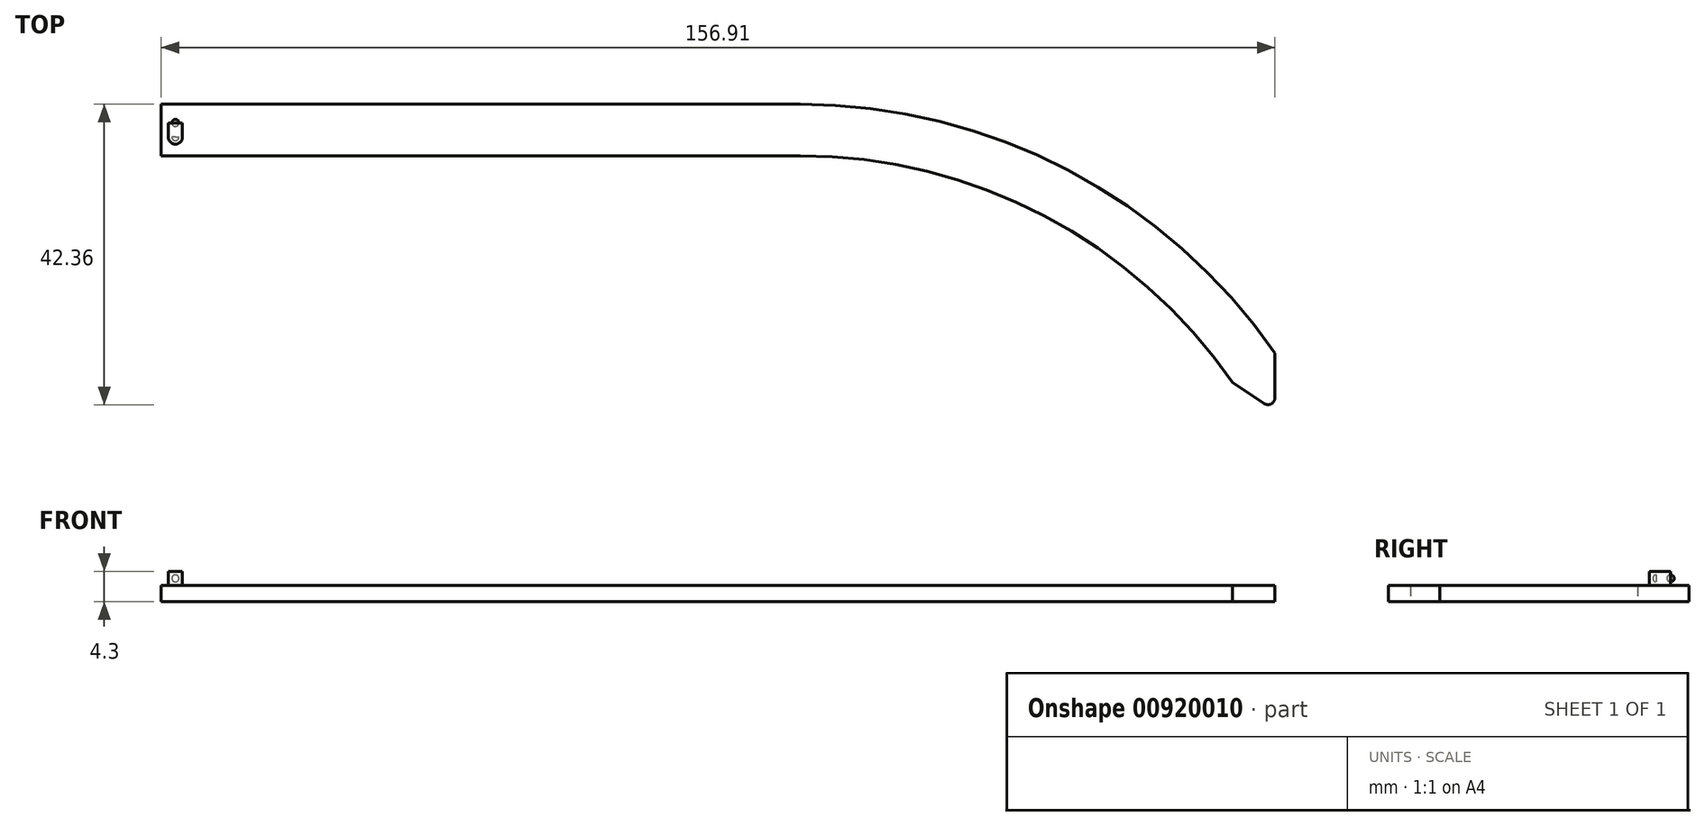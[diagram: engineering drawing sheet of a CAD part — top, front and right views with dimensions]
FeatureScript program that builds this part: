
annotation { "Feature Type Name" : "Feature", "Feature Type Description" : "" }
export const myFeature = defineFeature(function(context is Context, id is Id, definition is map)
    precondition{}
    {
        {
            var Q0;
            Q0=qCreatedBy(makeId("Top.planeOp"),FACE);
            var sketch = newSketch(context, id + "F0", { "sketchPlane" : qUnion([Q0])});
            skLineSegment(sketch, "E0.bottom", {"start": v(-45, 3.62) * mm, "end": v(45, 3.62) * mm});
            skLineSegment(sketch, "E0.top", {"start": v(-45, -3.62) * mm, "end": v(45, -3.62) * mm});
            skLineSegment(sketch, "E0.left", {"start": v(-45, 3.62) * mm, "end": v(-45, -3.62) * mm});
            skLineSegment(sketch, "E0.right", {"start": v(45, 3.62) * mm, "end": v(45, -3.62) * mm});
            skPoint(sketch, "E0.middle", {"position": v(0, 0) * mm});
            skLineSegment(sketch, "E1", {"start": v(45, 20.51) * mm, "end": v(45, -38.93) * mm});
            skArc(sketch, "E2", {"start": v(111.91, -31.5) * mm, "mid": v(82.79, -5.69) * mm, "end": v(45, 3.62) * mm});
            skArc(sketch, "E3.0", {"start": v(105.95, -35.62) * mm, "mid": v(79.42, -12.1) * mm, "end": v(45, -3.62) * mm});
            skLineSegment(sketch, "E4", {"start": v(105.95, -35.62) * mm, "end": v(110.36, -38.57) * mm});
            skLineSegment(sketch, "E5", {"start": v(111.91, -37.75) * mm, "end": v(111.91, -31.5) * mm});
            skPoint(sketch, "E6.visualSharp", {"position": v(111.91, -39.62) * mm});
            skArc(sketch, "E6.filletArc", {"start": v(110.36, -38.57) * mm, "mid": v(111.39, -38.63) * mm, "end": v(111.91, -37.75) * mm});
            skLineSegment(sketch, "E7", {"start": v(-45, 0) * mm, "end": v(-44, 0) * mm});
            skLineSegment(sketch, "E8", {"start": v(-44, 0) * mm, "end": v(-43, 0) * mm});
            skLineSegment(sketch, "E9.bottom", {"start": v(-42, 1) * mm, "end": v(-44, 1) * mm});
            skLineSegment(sketch, "E9.top", {"start": v(-42, -1) * mm, "end": v(-44, -1) * mm});
            skLineSegment(sketch, "E9.left", {"start": v(-42, 1) * mm, "end": v(-42, -1) * mm});
            skLineSegment(sketch, "E9.right", {"start": v(-44, 1) * mm, "end": v(-44, -1) * mm});
            skPoint(sketch, "E9.middle", {"position": v(-43, 0) * mm});
            skSolve(sketch);
        }
        {
            var Q0;
            {var subQ6=sQuery(id+"F0.wireOp",EDGE,"E0.bottom");Q0=makeQuery(id+"F0.imprint","IMPRINT",FACE,{"disambiguationData":[TD([[makeQuery(id+"F0.imprint","IMPRINT",EDGE,{"derivedFrom":subQ6}),-1.0]])]});}
            var Q1;
            Q1=makeQuery(id+"F0.imprint","IMPRINT",FACE,{"disambiguationData":[TD([[makeQuery(id+"F0.imprint","IMPRINT",EDGE,{"derivedFrom":sQuery(id+"F0.wireOp",EDGE,"E0.right")}),1.0]])]});
            var Q2;
            {var subQ3=sQuery(id+"F0.wireOp",EDGE,"E9.bottom");Q2=makeQuery(id+"F0.imprint","IMPRINT",FACE,{"disambiguationData":[TD([[makeQuery(id+"F0.imprint","IMPRINT",EDGE,{"derivedFrom":subQ3}),1.0]])]});}
            extrude(context, id + "F1", {"entities" : qUnion([Q0, Q1, Q2]), "depth" : 2.3 * mm, "offsetDistance" : 25 * mm});
        }
        {
            var Q0;
            Q0=makeQuery(id+"F1.opExtrude","CAP_FACE",FACE,{"disambiguationData":[OSD([sQuery(id+"F0.wireOp",EDGE,"E0.bottom"),sQuery(id+"F0.wireOp",EDGE,"E0.top"),sQuery(id+"F0.wireOp",EDGE,"E0.left"),sQuery(id+"F0.wireOp",EDGE,"E2"),sQuery(id+"F0.wireOp",EDGE,"E3.0"),sQuery(id+"F0.wireOp",EDGE,"E4"),sQuery(id+"F0.wireOp",EDGE,"E5"),sQuery(id+"F0.wireOp",EDGE,"E6.filletArc")])],"isStart":false});
            var sketch = newSketch(context, id + "F2", { "sketchPlane" : qUnion([Q0])});
            skLineSegment(sketch, "E10", {"start": v(-45, 0) * mm, "end": v(-43, 0) * mm});
            skLineSegment(sketch, "E11.bottom", {"start": v(-42, 1) * mm, "end": v(-44, 1) * mm});
            skLineSegment(sketch, "E11.top", {"start": v(-42, -1) * mm, "end": v(-44, -1) * mm});
            skLineSegment(sketch, "E11.left", {"start": v(-42, 1) * mm, "end": v(-42, -1) * mm});
            skLineSegment(sketch, "E11.right", {"start": v(-44, 1) * mm, "end": v(-44, -1) * mm});
            skPoint(sketch, "E11.middle", {"position": v(-43, 0) * mm});
            skSolve(sketch);
        }
        {
            var Q0;
            {var subQ1=sQuery(id+"F2.wireOp",EDGE,"E11.bottom");Q0=makeQuery(id+"F2.imprint","IMPRINT",FACE,{"disambiguationData":[TD([[makeQuery(id+"F2.imprint","IMPRINT",EDGE,{"derivedFrom":subQ1}),1.0]])]});}
            extrude(context, id + "F3", {"entities" : qUnion([Q0]), "operationType" : NewBodyOperationType.ADD, "depth" : 2 * mm, "offsetDistance" : 25 * mm});
        }
        {
            var Q0;
            Q0=makeQuery(id+"F3.opExtrude","SWEPT_FACE",FACE,{"disambiguationData":[OSD([sQuery(id+"F2.wireOp",EDGE,"E11.bottom")])]});
            var sketch = newSketch(context, id + "F4", { "sketchPlane" : qUnion([Q0])});
            skLineSegment(sketch, "E12", {"start": v(44, 3.3) * mm, "end": v(42, 3.3) * mm});
            skLineSegment(sketch, "E13", {"start": v(43, 4.3) * mm, "end": v(43, 2.3) * mm});
            skArc(sketch, "E14", {"start": v(43, 3.8) * mm, "mid": v(43.5, 3.3) * mm, "end": v(43, 2.8) * mm});
            skSolve(sketch);
        }
        {
            var Q0;
            {var subQ0=sQuery(id+"F4.wireOp",EDGE,"E14");var subQ1=sQuery(id+"F4.wireOp",EDGE,"E12");var subQ2=makeQuery(id+"F4.imprint","INTERSECT",VERTEX,{"derivedFrom":[subQ1,subQ0]});Q0=makeQuery(id+"F4.imprint","IMPRINT",FACE,{"disambiguationData":[TD([[makeQuery(id+"F4.imprint","IMPRINT",EDGE,{"disambiguationData":[TD([[subQ2,-1.0]])],"derivedFrom":subQ1}),-1.0]])]});}
            var Q1;
            {var subQ0=sQuery(id+"F4.wireOp",EDGE,"E14");var subQ1=sQuery(id+"F4.wireOp",EDGE,"E12");var subQ2=makeQuery(id+"F4.imprint","INTERSECT",VERTEX,{"derivedFrom":[subQ1,subQ0]});Q1=makeQuery(id+"F4.imprint","IMPRINT",FACE,{"disambiguationData":[TD([[makeQuery(id+"F4.imprint","IMPRINT",EDGE,{"disambiguationData":[TD([[subQ2,-1.0]])],"derivedFrom":subQ1}),1.0]])]});}
            var Q2;
            Q2=sQuery(id+"F4.wireOp",EDGE,"E13");
            revolve(context, id + "F5", {"surfaceOperationType" : NewSurfaceOperationType.NEW, "entities" : qUnion([Q0, Q1]), "axis" : qUnion([Q2]), "revolveType" : RevolveType.FULL});
        }
        {
            var Q0;
            Q0=makeQuery(id+"F3.opExtrude","SWEPT_FACE",FACE,{"disambiguationData":[OSD([sQuery(id+"F2.wireOp",EDGE,"E11.top")])]});
            var sketch = newSketch(context, id + "F6", { "sketchPlane" : qUnion([Q0])});
            skLineSegment(sketch, "E15", {"start": v(-43, 4.3) * mm, "end": v(-43, 2.3) * mm});
            skLineSegment(sketch, "E16", {"start": v(-44, 3.3) * mm, "end": v(-42, 3.3) * mm});
            skArc(sketch, "E17", {"start": v(-43, 3.8) * mm, "mid": v(-42.5, 3.3) * mm, "end": v(-43, 2.8) * mm});
            skSolve(sketch);
        }
        {
            var Q0;
            {var subQ0=sQuery(id+"F6.wireOp",EDGE,"E17");var subQ1=sQuery(id+"F6.wireOp",EDGE,"E15");var subQ2=makeQuery(id+"F6.imprint","INTERSECT",VERTEX,{"disambiguationData":[OD(0.0)],"derivedFrom":[subQ1,subQ0]});Q0=makeQuery(id+"F6.imprint","IMPRINT",FACE,{"disambiguationData":[TD([[makeQuery(id+"F6.imprint","IMPRINT",EDGE,{"disambiguationData":[TD([[subQ2,-1.0]])],"derivedFrom":subQ1}),1.0]])]});}
            var Q1;
            {var subQ0=sQuery(id+"F6.wireOp",EDGE,"E17");var subQ1=sQuery(id+"F6.wireOp",EDGE,"E15");var subQ2=makeQuery(id+"F6.imprint","INTERSECT",VERTEX,{"disambiguationData":[OD(1.0)],"derivedFrom":[subQ1,subQ0]});Q1=makeQuery(id+"F6.imprint","IMPRINT",FACE,{"disambiguationData":[TD([[makeQuery(id+"F6.imprint","IMPRINT",EDGE,{"disambiguationData":[TD([[subQ2,1.0]])],"derivedFrom":subQ1}),1.0]])]});}
            var Q2;
            Q2=sQuery(id+"F6.wireOp",EDGE,"E15");
            revolve(context, id + "F7", {"operationType" : NewBodyOperationType.ADD, "surfaceOperationType" : NewSurfaceOperationType.NEW, "entities" : qUnion([Q0, Q1]), "axis" : qUnion([Q2]), "revolveType" : RevolveType.FULL});
        }
    });
